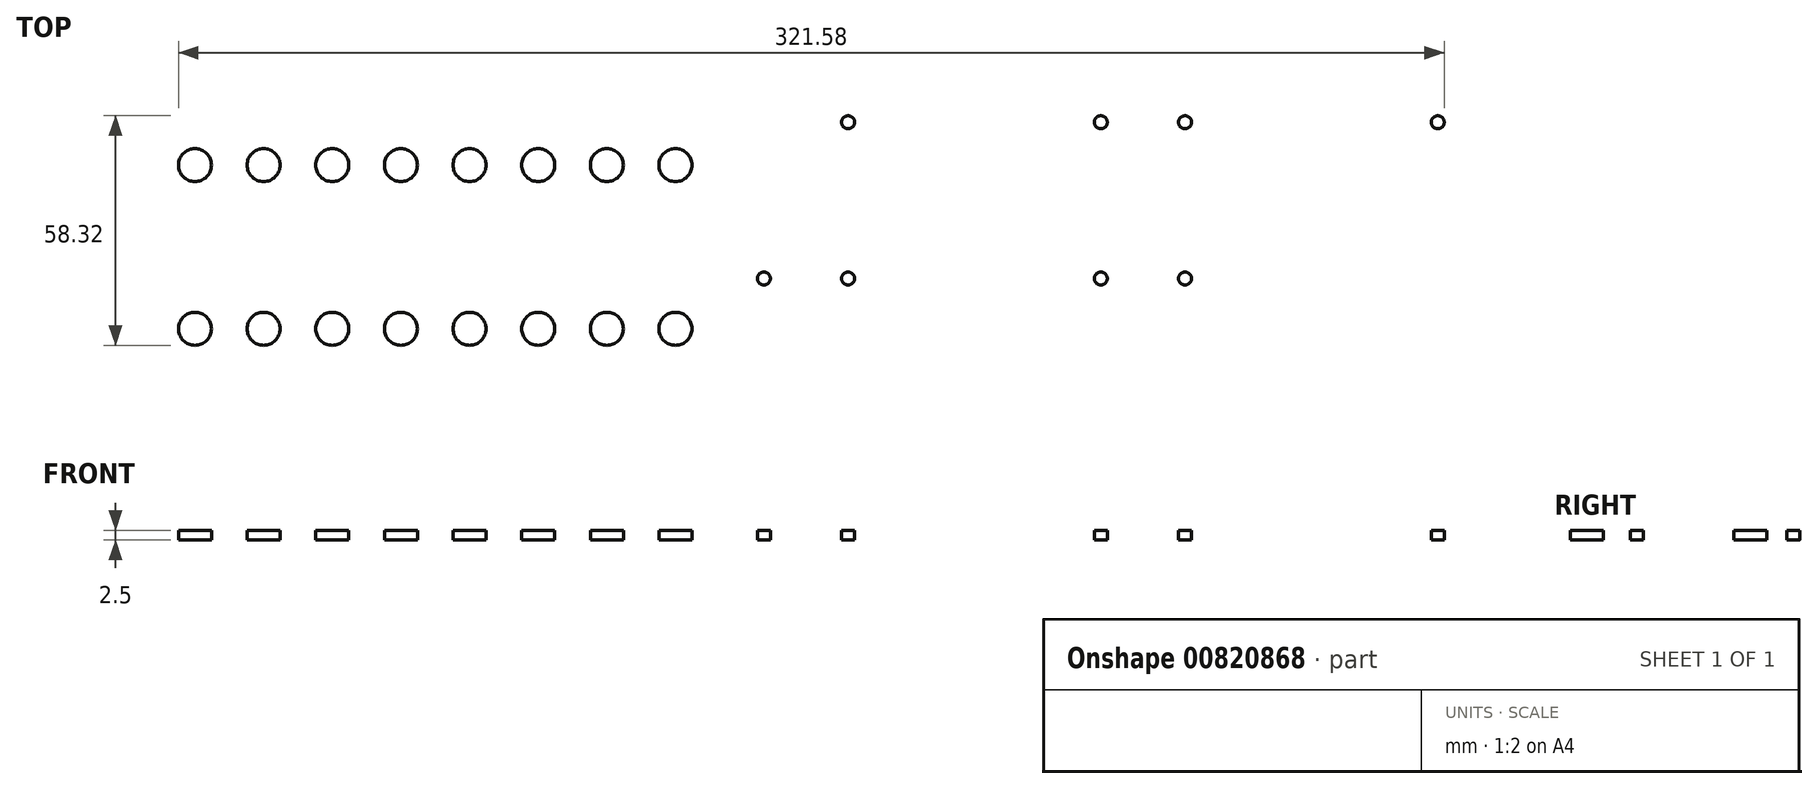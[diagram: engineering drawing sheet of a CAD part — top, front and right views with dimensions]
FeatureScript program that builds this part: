
annotation { "Feature Type Name" : "Feature", "Feature Type Description" : "" }
export const myFeature = defineFeature(function(context is Context, id is Id, definition is map)
    precondition{}
    {
        {
            var Q0;
            Q0=qCreatedBy(makeId("Top.planeOp"),FACE);
            var sketch = newSketch(context, id + "F0", { "sketchPlane" : qUnion([Q0])});
            skLineSegment(sketch, "E0.bottom", {"start": v(-66.95, 52.35) * mm, "end": v(415.65, 52.35) * mm});
            skLineSegment(sketch, "E0.top", {"start": v(-66.95, -36.55) * mm, "end": v(415.65, -36.55) * mm});
            skLineSegment(sketch, "E0.left", {"start": v(-66.95, 52.35) * mm, "end": v(-66.95, -36.55) * mm});
            skLineSegment(sketch, "E0.right", {"start": v(415.65, 52.35) * mm, "end": v(415.65, -36.55) * mm});
            skSolve(sketch);
        }
        {
            var Q0;
            Q0=makeQuery(id+"F0.imprint","IMPRINT",FACE,{"disambiguationData":[TD([[makeQuery(id+"F0.imprint","IMPRINT",EDGE,{"derivedFrom":sQuery(id+"F0.wireOp",EDGE,"E0.bottom")}),-1.0]])]});
            extrude(context, id + "F1", {"entities" : qUnion([Q0]), "depth" : 3 * mm, "offsetDistance" : 25 * mm});
        }
        {
            var Q0;
            Q0=makeQuery(id+"F1.opExtrude","CAP_FACE",FACE,{"disambiguationData":[OSD([sQuery(id+"F0.wireOp",EDGE,"E0.bottom"),sQuery(id+"F0.wireOp",EDGE,"E0.top"),sQuery(id+"F0.wireOp",EDGE,"E0.left"),sQuery(id+"F0.wireOp",EDGE,"E0.right")])],"isStart":false});
            var sketch = newSketch(context, id + "F2", { "sketchPlane" : qUnion([Q0])});
            skLineSegment(sketch, "E1.MirrorCS", {"start": v(-59.01, -1.97) * mm, "end": v(-61.51, -1.97) * mm});
            skLineSegment(sketch, "E2.MirrorCS", {"start": v(-59.01, -17.85) * mm, "end": v(-61.51, -17.85) * mm});
            skLineSegment(sketch, "E3.MirrorCS", {"start": v(-59.01, -17.85) * mm, "end": v(-56.51, -17.85) * mm});
            skLineSegment(sketch, "E4.MirrorCS", {"start": v(-59.01, -10.85) * mm, "end": v(-56.51, -10.85) * mm});
            skLineSegment(sketch, "E5.MirrorCS", {"start": v(-59.01, -10.85) * mm, "end": v(-61.51, -10.85) * mm});
            skLineSegment(sketch, "E6.MirrorCS", {"start": v(-59.01, -1.97) * mm, "end": v(-56.51, -1.97) * mm});
            skLineSegment(sketch, "E7.MirrorCS", {"start": v(-59.01, 5.03) * mm, "end": v(-61.51, 5.03) * mm});
            skLineSegment(sketch, "E8.MirrorCS", {"start": v(-59.01, 5.03) * mm, "end": v(-56.51, 5.03) * mm});
            skArc(sketch, "E9.MirrorCS", {"start": v(-61.51, -17.85) * mm, "mid": v(-64.01, -14.35) * mm, "end": v(-61.51, -10.85) * mm});
            skLineSegment(sketch, "E10.MirrorCS", {"start": v(-59.01, 49.5) * mm, "end": v(-61.51, 49.5) * mm});
            skArc(sketch, "E11.MirrorCS", {"start": v(-61.51, 33.62) * mm, "mid": v(-64.01, 30.12) * mm, "end": v(-61.51, 26.62) * mm});
            skPoint(sketch, "E12.MirrorP", {"position": v(-59.01, 1.55) * mm});
            skLineSegment(sketch, "E13.MirrorCS", {"start": v(-59.01, 17.75) * mm, "end": v(-56.51, 17.75) * mm});
            skLineSegment(sketch, "E14.MirrorCS", {"start": v(-59.01, 10.75) * mm, "end": v(-61.51, 10.75) * mm});
            skLineSegment(sketch, "E15.MirrorCS", {"start": v(-59.01, 17.75) * mm, "end": v(-61.51, 17.75) * mm});
            skPoint(sketch, "E16.MirrorP", {"position": v(-59.01, -14.33) * mm});
            skLineSegment(sketch, "E17.MirrorCS", {"start": v(-59.01, 49.5) * mm, "end": v(-56.51, 49.5) * mm});
            skLineSegment(sketch, "E18.MirrorCS", {"start": v(-59.01, 10.75) * mm, "end": v(-56.51, 10.75) * mm});
            skLineSegment(sketch, "E19.MirrorCS", {"start": v(-59.01, -26.72) * mm, "end": v(-56.51, -26.72) * mm});
            skLineSegment(sketch, "E20.MirrorCS", {"start": v(-59.01, 33.62) * mm, "end": v(-61.51, 33.62) * mm});
            skLineSegment(sketch, "E21.MirrorCS", {"start": v(-59.01, 26.62) * mm, "end": v(-56.51, 26.62) * mm});
            skPoint(sketch, "E22.MirrorP", {"position": v(-59.01, 1.53) * mm});
            skLineSegment(sketch, "E23.MirrorCS", {"start": v(-59.01, 33.62) * mm, "end": v(-56.51, 33.62) * mm});
            skLineSegment(sketch, "E24.MirrorCS", {"start": v(-59.01, -26.72) * mm, "end": v(-61.51, -26.72) * mm});
            skLineSegment(sketch, "E25.MirrorCS", {"start": v(-59.01, 26.62) * mm, "end": v(-61.51, 26.62) * mm});
            skArc(sketch, "E26.MirrorCS", {"start": v(-56.51, -10.85) * mm, "mid": v(-54.01, -14.35) * mm, "end": v(-56.51, -17.85) * mm});
            skPoint(sketch, "E27.MirrorP", {"position": v(-59.01, 30.12) * mm});
            skArc(sketch, "E28.MirrorCS", {"start": v(-56.51, -1.97) * mm, "mid": v(-54.01, 1.53) * mm, "end": v(-56.51, 5.03) * mm});
            skPoint(sketch, "E29.MirrorP", {"position": v(-59.01, -30.22) * mm});
            skArc(sketch, "E30.MirrorCS", {"start": v(-56.51, 26.62) * mm, "mid": v(-54.01, 30.12) * mm, "end": v(-56.51, 33.62) * mm});
            skLineSegment(sketch, "E31.MirrorCS", {"start": v(-59.01, -33.72) * mm, "end": v(-56.51, -33.72) * mm});
            skLineSegment(sketch, "E32.MirrorCS", {"start": v(-59.01, 42.5) * mm, "end": v(-61.51, 42.5) * mm});
            skLineSegment(sketch, "E33.MirrorCS", {"start": v(-59.01, 42.5) * mm, "end": v(-56.51, 42.5) * mm});
            skPoint(sketch, "E34.MirrorP", {"position": v(-59.01, -14.35) * mm});
            skLineSegment(sketch, "E35.MirrorCS", {"start": v(-59.01, -33.72) * mm, "end": v(-61.51, -33.72) * mm});
            skArc(sketch, "E36.MirrorCS", {"start": v(-61.51, 5.03) * mm, "mid": v(-64.01, 1.53) * mm, "end": v(-61.51, -1.97) * mm});
            skPoint(sketch, "E37.MirrorP", {"position": v(-59.01, 14.25) * mm});
            skPoint(sketch, "E38.MirrorP", {"position": v(1.07, 19.02) * mm});
            skCircle(sketch, "E39.MirrorC", {"center": v(170.96, 29.9) * mm, "radius": 1.65 * mm});
            skCircle(sketch, "E40.MirrorC", {"center": v(192.36, -9.8) * mm, "radius": 1.65 * mm});
            skCircle(sketch, "E41.MirrorC", {"center": v(256.56, -9.8) * mm, "radius": 1.65 * mm});
            skArc(sketch, "E42.MirrorCS", {"start": v(-56.51, 17.75) * mm, "mid": v(-54.01, 14.25) * mm, "end": v(-56.51, 10.75) * mm});
            skPoint(sketch, "E43.MirrorP", {"position": v(-16.37, 39.58) * mm});
            skCircle(sketch, "E44.MirrorC", {"center": v(170.96, -9.8) * mm, "radius": 1.65 * mm});
            skCircle(sketch, "E45.MirrorC", {"center": v(299.36, 29.9) * mm, "radius": 1.65 * mm});
            skCircle(sketch, "E46.MirrorC", {"center": v(149.56, -9.8) * mm, "radius": 1.65 * mm});
            skPoint(sketch, "E47.MirrorP", {"position": v(-16.37, 19.02) * mm});
            skPoint(sketch, "E48.MirrorP", {"position": v(1.07, -22.57) * mm});
            skPoint(sketch, "E49.MirrorP", {"position": v(1.07, 39.58) * mm});
            skCircle(sketch, "E50.MirrorC", {"center": v(128.16, -9.8) * mm, "radius": 1.65 * mm});
            skCircle(sketch, "E51.MirrorC", {"center": v(277.96, 29.9) * mm, "radius": 1.65 * mm});
            skCircle(sketch, "E52.MirrorC", {"center": v(192.36, 29.9) * mm, "radius": 1.65 * mm});
            skCircle(sketch, "E53.MirrorC", {"center": v(213.76, 29.9) * mm, "radius": 1.65 * mm});
            skPoint(sketch, "E54.MirrorP", {"position": v(-16.37, -2.01) * mm});
            skPoint(sketch, "E55.MirrorP", {"position": v(1.07, -2.01) * mm});
            skPoint(sketch, "E56.MirrorP", {"position": v(-59.01, 46) * mm});
            skCircle(sketch, "E57.MirrorC", {"center": v(213.76, -9.8) * mm, "radius": 1.65 * mm});
            skCircle(sketch, "E58.MirrorC", {"center": v(235.16, -9.8) * mm, "radius": 1.65 * mm});
            skCircle(sketch, "E59.MirrorC", {"center": v(235.16, 29.9) * mm, "radius": 1.65 * mm});
            skPoint(sketch, "E60.MirrorP", {"position": v(-59.01, -30.2) * mm});
            skPoint(sketch, "E61.MirrorP", {"position": v(-16.37, -22.57) * mm});
            skCircle(sketch, "E62.MirrorC", {"center": v(149.56, 29.9) * mm, "radius": 1.65 * mm});
            skCircle(sketch, "E63.MirrorC", {"center": v(256.56, 29.9) * mm, "radius": 1.65 * mm});
            skCircle(sketch, "E64.MirrorC", {"center": v(277.96, -9.8) * mm, "radius": 1.65 * mm});
            skCircle(sketch, "E65.MirrorC", {"center": v(35.95, 19.02) * mm, "radius": 4.2 * mm});
            skPoint(sketch, "E66.MirrorP", {"position": v(88.27, -22.57) * mm});
            skArc(sketch, "E67.MirrorCS", {"start": v(-56.51, -33.72) * mm, "mid": v(-54.01, -30.22) * mm, "end": v(-56.51, -26.72) * mm});
            skCircle(sketch, "E68.MirrorC", {"center": v(53.39, 39.58) * mm, "radius": 4.2 * mm});
            skPoint(sketch, "E69.MirrorP", {"position": v(105.7, 19.02) * mm});
            skPoint(sketch, "E70.MirrorP", {"position": v(18.5, 39.58) * mm});
            skCircle(sketch, "E71.MirrorC", {"center": v(-16.37, -2.01) * mm, "radius": 4.2 * mm});
            skCircle(sketch, "E72.MirrorC", {"center": v(-16.37, 39.58) * mm, "radius": 4.2 * mm});
            skCircle(sketch, "E73.MirrorC", {"center": v(-16.37, -22.57) * mm, "radius": 4.2 * mm});
            skCircle(sketch, "E74.MirrorC", {"center": v(1.07, -22.57) * mm, "radius": 4.2 * mm});
            skPoint(sketch, "E75.MirrorP", {"position": v(105.7, -2.01) * mm});
            skCircle(sketch, "E76.MirrorC", {"center": v(88.27, 19.02) * mm, "radius": 4.2 * mm});
            skCircle(sketch, "E77.MirrorC", {"center": v(35.95, 39.58) * mm, "radius": 4.2 * mm});
            skPoint(sketch, "E78.MirrorP", {"position": v(70.83, -2.01) * mm});
            skPoint(sketch, "E79.MirrorP", {"position": v(18.5, -2.01) * mm});
            skCircle(sketch, "E80.MirrorC", {"center": v(1.07, 19.02) * mm, "radius": 4.2 * mm});
            skArc(sketch, "E81.MirrorCS", {"start": v(-56.51, 49.5) * mm, "mid": v(-54.01, 46) * mm, "end": v(-56.51, 42.5) * mm});
            skCircle(sketch, "E82.MirrorC", {"center": v(35.95, -22.57) * mm, "radius": 4.2 * mm});
            skCircle(sketch, "E83.MirrorC", {"center": v(70.83, 39.58) * mm, "radius": 4.2 * mm});
            skPoint(sketch, "E84.MirrorP", {"position": v(70.83, 19.02) * mm});
            skPoint(sketch, "E85.MirrorP", {"position": v(53.39, -22.57) * mm});
            skCircle(sketch, "E86.MirrorC", {"center": v(-16.37, 19.02) * mm, "radius": 4.2 * mm});
            skArc(sketch, "E87.MirrorCS", {"start": v(-61.51, 10.75) * mm, "mid": v(-64.01, 14.25) * mm, "end": v(-61.51, 17.75) * mm});
            skArc(sketch, "E88.MirrorCS", {"start": v(-61.51, 42.5) * mm, "mid": v(-64.01, 46) * mm, "end": v(-61.51, 49.5) * mm});
            skCircle(sketch, "E89.MirrorC", {"center": v(70.83, 19.02) * mm, "radius": 4.2 * mm});
            skCircle(sketch, "E90.MirrorC", {"center": v(105.7, 19.02) * mm, "radius": 4.2 * mm});
            skCircle(sketch, "E91.MirrorC", {"center": v(88.27, 39.58) * mm, "radius": 4.2 * mm});
            skCircle(sketch, "E92.MirrorC", {"center": v(105.7, -22.57) * mm, "radius": 4.2 * mm});
            skPoint(sketch, "E93.MirrorP", {"position": v(88.27, -2.01) * mm});
            skArc(sketch, "E94.MirrorCS", {"start": v(-61.51, -26.72) * mm, "mid": v(-64.01, -30.22) * mm, "end": v(-61.51, -33.72) * mm});
            skCircle(sketch, "E95.MirrorC", {"center": v(88.27, -22.57) * mm, "radius": 4.2 * mm});
            skCircle(sketch, "E96.MirrorC", {"center": v(53.39, -22.57) * mm, "radius": 4.2 * mm});
            skPoint(sketch, "E97.MirrorP", {"position": v(53.39, -2.01) * mm});
            skPoint(sketch, "E98.MirrorP", {"position": v(35.95, -2.01) * mm});
            skCircle(sketch, "E99.MirrorC", {"center": v(18.5, 19.02) * mm, "radius": 4.2 * mm});
            skPoint(sketch, "E100.MirrorP", {"position": v(18.5, -22.57) * mm});
            skCircle(sketch, "E101.MirrorC", {"center": v(70.83, -22.57) * mm, "radius": 4.2 * mm});
            skCircle(sketch, "E102.MirrorC", {"center": v(88.27, -2.01) * mm, "radius": 4.2 * mm});
            skCircle(sketch, "E103.MirrorC", {"center": v(105.7, -2.01) * mm, "radius": 4.2 * mm});
            skPoint(sketch, "E104.MirrorP", {"position": v(53.39, 19.02) * mm});
            skCircle(sketch, "E105.MirrorC", {"center": v(1.07, 39.58) * mm, "radius": 4.2 * mm});
            skCircle(sketch, "E106.MirrorC", {"center": v(53.39, -2.01) * mm, "radius": 4.2 * mm});
            skCircle(sketch, "E107.MirrorC", {"center": v(70.83, -2.01) * mm, "radius": 4.2 * mm});
            skCircle(sketch, "E108.MirrorC", {"center": v(18.5, 39.58) * mm, "radius": 4.2 * mm});
            skCircle(sketch, "E109.MirrorC", {"center": v(105.7, 39.58) * mm, "radius": 4.2 * mm});
            skCircle(sketch, "E110.MirrorC", {"center": v(35.95, -2.01) * mm, "radius": 4.2 * mm});
            skCircle(sketch, "E111.MirrorC", {"center": v(18.5, -2.01) * mm, "radius": 4.2 * mm});
            skCircle(sketch, "E112.MirrorC", {"center": v(1.07, -2.01) * mm, "radius": 4.2 * mm});
            skCircle(sketch, "E113.MirrorC", {"center": v(18.5, -22.57) * mm, "radius": 4.2 * mm});
            skCircle(sketch, "E114.MirrorC", {"center": v(53.39, 19.02) * mm, "radius": 4.2 * mm});
            skLineSegment(sketch, "E115.MirrorCS", {"start": v(407.71, 5.03) * mm, "end": v(405.21, 5.03) * mm});
            skLineSegment(sketch, "E116.MirrorCS", {"start": v(407.71, 5.03) * mm, "end": v(410.21, 5.03) * mm});
            skLineSegment(sketch, "E117.MirrorCS", {"start": v(407.71, -10.85) * mm, "end": v(405.21, -10.85) * mm});
            skLineSegment(sketch, "E118.MirrorCS", {"start": v(407.71, -10.85) * mm, "end": v(410.21, -10.85) * mm});
            skLineSegment(sketch, "E119.MirrorCS", {"start": v(407.71, -1.97) * mm, "end": v(410.21, -1.97) * mm});
            skLineSegment(sketch, "E120.MirrorCS", {"start": v(407.71, -17.85) * mm, "end": v(410.21, -17.85) * mm});
            skLineSegment(sketch, "E121.MirrorCS", {"start": v(407.71, -1.97) * mm, "end": v(405.21, -1.97) * mm});
            skLineSegment(sketch, "E122.MirrorCS", {"start": v(407.71, -17.85) * mm, "end": v(405.21, -17.85) * mm});
            skPoint(sketch, "E123.MirrorP", {"position": v(407.71, 1.55) * mm});
            skArc(sketch, "E124.MirrorCS", {"start": v(410.21, -17.85) * mm, "mid": v(412.71, -14.35) * mm, "end": v(410.21, -10.85) * mm});
            skLineSegment(sketch, "E125.MirrorCS", {"start": v(407.71, -26.72) * mm, "end": v(405.21, -26.72) * mm});
            skLineSegment(sketch, "E126.MirrorCS", {"start": v(407.71, -33.72) * mm, "end": v(410.21, -33.72) * mm});
            skPoint(sketch, "E127.MirrorP", {"position": v(407.71, -14.33) * mm});
            skArc(sketch, "E128.MirrorCS", {"start": v(410.21, 33.62) * mm, "mid": v(412.71, 30.12) * mm, "end": v(410.21, 26.62) * mm});
            skLineSegment(sketch, "E129.MirrorCS", {"start": v(407.71, -33.72) * mm, "end": v(405.21, -33.72) * mm});
            skLineSegment(sketch, "E130.MirrorCS", {"start": v(407.71, -26.72) * mm, "end": v(410.21, -26.72) * mm});
            skLineSegment(sketch, "E131.MirrorCS", {"start": v(407.71, 42.5) * mm, "end": v(410.21, 42.5) * mm});
            skLineSegment(sketch, "E132.MirrorCS", {"start": v(407.71, 42.5) * mm, "end": v(405.21, 42.5) * mm});
            skLineSegment(sketch, "E133.MirrorCS", {"start": v(407.71, 10.75) * mm, "end": v(405.21, 10.75) * mm});
            skPoint(sketch, "E134.MirrorP", {"position": v(407.71, -14.35) * mm});
            skLineSegment(sketch, "E135.MirrorCS", {"start": v(407.71, 49.5) * mm, "end": v(405.21, 49.5) * mm});
            skPoint(sketch, "E136.MirrorP", {"position": v(407.71, -30.2) * mm});
            skLineSegment(sketch, "E137.MirrorCS", {"start": v(407.71, 33.62) * mm, "end": v(410.21, 33.62) * mm});
            skLineSegment(sketch, "E138.MirrorCS", {"start": v(407.71, 10.75) * mm, "end": v(410.21, 10.75) * mm});
            skLineSegment(sketch, "E139.MirrorCS", {"start": v(407.71, 17.75) * mm, "end": v(410.21, 17.75) * mm});
            skLineSegment(sketch, "E140.MirrorCS", {"start": v(407.71, 17.75) * mm, "end": v(405.21, 17.75) * mm});
            skLineSegment(sketch, "E141.MirrorCS", {"start": v(407.71, 33.62) * mm, "end": v(405.21, 33.62) * mm});
            skLineSegment(sketch, "E142.MirrorCS", {"start": v(407.71, 26.62) * mm, "end": v(405.21, 26.62) * mm});
            skLineSegment(sketch, "E143.MirrorCS", {"start": v(407.71, 49.5) * mm, "end": v(410.21, 49.5) * mm});
            skLineSegment(sketch, "E144.MirrorCS", {"start": v(407.71, 26.62) * mm, "end": v(410.21, 26.62) * mm});
            skPoint(sketch, "E145.MirrorP", {"position": v(407.71, 1.53) * mm});
            skArc(sketch, "E146.MirrorCS", {"start": v(405.21, -33.72) * mm, "mid": v(402.71, -30.22) * mm, "end": v(405.21, -26.72) * mm});
            skPoint(sketch, "E147.MirrorP", {"position": v(407.71, 46) * mm});
            skPoint(sketch, "E148.MirrorP", {"position": v(407.71, 14.25) * mm});
            skArc(sketch, "E149.MirrorCS", {"start": v(410.21, 10.75) * mm, "mid": v(412.71, 14.25) * mm, "end": v(410.21, 17.75) * mm});
            skPoint(sketch, "E150.MirrorP", {"position": v(407.71, 30.12) * mm});
            skArc(sketch, "E151.MirrorCS", {"start": v(405.21, -1.97) * mm, "mid": v(402.71, 1.53) * mm, "end": v(405.21, 5.03) * mm});
            skArc(sketch, "E152.MirrorCS", {"start": v(405.21, -10.85) * mm, "mid": v(402.71, -14.35) * mm, "end": v(405.21, -17.85) * mm});
            skArc(sketch, "E153.MirrorCS", {"start": v(405.21, 49.5) * mm, "mid": v(402.71, 46) * mm, "end": v(405.21, 42.5) * mm});
            skArc(sketch, "E154.MirrorCS", {"start": v(410.21, -26.72) * mm, "mid": v(412.71, -30.22) * mm, "end": v(410.21, -33.72) * mm});
            skArc(sketch, "E155.MirrorCS", {"start": v(405.21, 26.62) * mm, "mid": v(402.71, 30.12) * mm, "end": v(405.21, 33.62) * mm});
            skArc(sketch, "E156.MirrorCS", {"start": v(410.21, 42.5) * mm, "mid": v(412.71, 46) * mm, "end": v(410.21, 49.5) * mm});
            skArc(sketch, "E157.MirrorCS", {"start": v(405.21, 17.75) * mm, "mid": v(402.71, 14.25) * mm, "end": v(405.21, 10.75) * mm});
            skArc(sketch, "E158.MirrorCS", {"start": v(410.21, 5.03) * mm, "mid": v(412.71, 1.53) * mm, "end": v(410.21, -1.97) * mm});
            skPoint(sketch, "E159.MirrorP", {"position": v(407.71, -30.22) * mm});
            skSolve(sketch);
        }
        {
            var Q0;
            Q0=makeQuery(id+"F2.imprint","IMPRINT",FACE,{"disambiguationData":[TD([[makeQuery(id+"F2.imprint","IMPRINT",EDGE,{"derivedFrom":sQuery(id+"F2.wireOp",EDGE,"E19.MirrorCS")}),-1.0]])]});
            var Q1;
            Q1=makeQuery(id+"F2.imprint","IMPRINT",FACE,{"disambiguationData":[TD([[makeQuery(id+"F2.imprint","IMPRINT",EDGE,{"derivedFrom":sQuery(id+"F2.wireOp",EDGE,"E10.MirrorCS")}),1.0]])]});
            var Q2;
            Q2=makeQuery(id+"F2.imprint","IMPRINT",FACE,{"disambiguationData":[TD([[makeQuery(id+"F2.imprint","IMPRINT",EDGE,{"derivedFrom":sQuery(id+"F2.wireOp",EDGE,"E13.MirrorCS")}),-1.0]])]});
            var Q3;
            Q3=makeQuery(id+"F2.imprint","IMPRINT",FACE,{"disambiguationData":[TD([[makeQuery(id+"F2.imprint","IMPRINT",EDGE,{"derivedFrom":sQuery(id+"F2.wireOp",EDGE,"E2.MirrorCS")}),-1.0]])]});
            var Q4;
            Q4=makeQuery(id+"F2.imprint","IMPRINT",FACE,{"disambiguationData":[TD([[makeQuery(id+"F2.imprint","IMPRINT",EDGE,{"derivedFrom":sQuery(id+"F2.wireOp",EDGE,"E1.MirrorCS")}),-1.0]])]});
            var Q5;
            Q5=makeQuery(id+"F2.imprint","IMPRINT",FACE,{"disambiguationData":[TD([[makeQuery(id+"F2.imprint","IMPRINT",EDGE,{"derivedFrom":sQuery(id+"F2.wireOp",EDGE,"E20.MirrorCS")}),1.0]])]});
            var Q6;
            Q6=makeQuery(id+"F2.imprint","IMPRINT",FACE,{"disambiguationData":[TD([[makeQuery(id+"F2.imprint","IMPRINT",EDGE,{"derivedFrom":sQuery(id+"F2.wireOp",EDGE,"E83.MirrorC")}),1.0]])]});
            var Q7;
            Q7=makeQuery(id+"F2.imprint","IMPRINT",FACE,{"disambiguationData":[TD([[makeQuery(id+"F2.imprint","IMPRINT",EDGE,{"derivedFrom":sQuery(id+"F2.wireOp",EDGE,"E80.MirrorC")}),-1.0]])]});
            var Q8;
            Q8=makeQuery(id+"F2.imprint","IMPRINT",FACE,{"disambiguationData":[TD([[makeQuery(id+"F2.imprint","IMPRINT",EDGE,{"derivedFrom":sQuery(id+"F2.wireOp",EDGE,"E101.MirrorC")}),-1.0]])]});
            var Q9;
            Q9=makeQuery(id+"F2.imprint","IMPRINT",FACE,{"disambiguationData":[TD([[makeQuery(id+"F2.imprint","IMPRINT",EDGE,{"derivedFrom":sQuery(id+"F2.wireOp",EDGE,"E74.MirrorC")}),-1.0]])]});
            var Q10;
            Q10=makeQuery(id+"F2.imprint","IMPRINT",FACE,{"disambiguationData":[TD([[makeQuery(id+"F2.imprint","IMPRINT",EDGE,{"derivedFrom":sQuery(id+"F2.wireOp",EDGE,"E105.MirrorC")}),1.0]])]});
            var Q11;
            Q11=makeQuery(id+"F2.imprint","IMPRINT",FACE,{"disambiguationData":[TD([[makeQuery(id+"F2.imprint","IMPRINT",EDGE,{"derivedFrom":sQuery(id+"F2.wireOp",EDGE,"E107.MirrorC")}),1.0]])]});
            var Q12;
            Q12=makeQuery(id+"F2.imprint","IMPRINT",FACE,{"disambiguationData":[TD([[makeQuery(id+"F2.imprint","IMPRINT",EDGE,{"derivedFrom":sQuery(id+"F2.wireOp",EDGE,"E95.MirrorC")}),-1.0]])]});
            var Q13;
            Q13=makeQuery(id+"F2.imprint","IMPRINT",FACE,{"disambiguationData":[TD([[makeQuery(id+"F2.imprint","IMPRINT",EDGE,{"derivedFrom":sQuery(id+"F2.wireOp",EDGE,"E65.MirrorC")}),-1.0]])]});
            var Q14;
            Q14=makeQuery(id+"F2.imprint","IMPRINT",FACE,{"disambiguationData":[TD([[makeQuery(id+"F2.imprint","IMPRINT",EDGE,{"derivedFrom":sQuery(id+"F2.wireOp",EDGE,"E76.MirrorC")}),-1.0]])]});
            var Q15;
            Q15=makeQuery(id+"F2.imprint","IMPRINT",FACE,{"disambiguationData":[TD([[makeQuery(id+"F2.imprint","IMPRINT",EDGE,{"derivedFrom":sQuery(id+"F2.wireOp",EDGE,"E99.MirrorC")}),-1.0]])]});
            var Q16;
            Q16=makeQuery(id+"F2.imprint","IMPRINT",FACE,{"disambiguationData":[TD([[makeQuery(id+"F2.imprint","IMPRINT",EDGE,{"derivedFrom":sQuery(id+"F2.wireOp",EDGE,"E114.MirrorC")}),-1.0]])]});
            var Q17;
            Q17=makeQuery(id+"F2.imprint","IMPRINT",FACE,{"disambiguationData":[TD([[makeQuery(id+"F2.imprint","IMPRINT",EDGE,{"derivedFrom":sQuery(id+"F2.wireOp",EDGE,"E92.MirrorC")}),-1.0]])]});
            var Q18;
            Q18=makeQuery(id+"F2.imprint","IMPRINT",FACE,{"disambiguationData":[TD([[makeQuery(id+"F2.imprint","IMPRINT",EDGE,{"derivedFrom":sQuery(id+"F2.wireOp",EDGE,"E68.MirrorC")}),1.0]])]});
            var Q19;
            Q19=makeQuery(id+"F2.imprint","IMPRINT",FACE,{"disambiguationData":[TD([[makeQuery(id+"F2.imprint","IMPRINT",EDGE,{"derivedFrom":sQuery(id+"F2.wireOp",EDGE,"E72.MirrorC")}),1.0]])]});
            var Q20;
            Q20=makeQuery(id+"F2.imprint","IMPRINT",FACE,{"disambiguationData":[TD([[makeQuery(id+"F2.imprint","IMPRINT",EDGE,{"derivedFrom":sQuery(id+"F2.wireOp",EDGE,"E91.MirrorC")}),1.0]])]});
            var Q21;
            Q21=makeQuery(id+"F2.imprint","IMPRINT",FACE,{"disambiguationData":[TD([[makeQuery(id+"F2.imprint","IMPRINT",EDGE,{"derivedFrom":sQuery(id+"F2.wireOp",EDGE,"E113.MirrorC")}),-1.0]])]});
            var Q22;
            Q22=makeQuery(id+"F2.imprint","IMPRINT",FACE,{"disambiguationData":[TD([[makeQuery(id+"F2.imprint","IMPRINT",EDGE,{"derivedFrom":sQuery(id+"F2.wireOp",EDGE,"E106.MirrorC")}),1.0]])]});
            var Q23;
            Q23=makeQuery(id+"F2.imprint","IMPRINT",FACE,{"disambiguationData":[TD([[makeQuery(id+"F2.imprint","IMPRINT",EDGE,{"derivedFrom":sQuery(id+"F2.wireOp",EDGE,"E73.MirrorC")}),-1.0]])]});
            var Q24;
            Q24=makeQuery(id+"F2.imprint","IMPRINT",FACE,{"disambiguationData":[TD([[makeQuery(id+"F2.imprint","IMPRINT",EDGE,{"derivedFrom":sQuery(id+"F2.wireOp",EDGE,"E102.MirrorC")}),1.0]])]});
            var Q25;
            Q25=makeQuery(id+"F2.imprint","IMPRINT",FACE,{"disambiguationData":[TD([[makeQuery(id+"F2.imprint","IMPRINT",EDGE,{"derivedFrom":sQuery(id+"F2.wireOp",EDGE,"E96.MirrorC")}),-1.0]])]});
            var Q26;
            Q26=makeQuery(id+"F2.imprint","IMPRINT",FACE,{"disambiguationData":[TD([[makeQuery(id+"F2.imprint","IMPRINT",EDGE,{"derivedFrom":sQuery(id+"F2.wireOp",EDGE,"E77.MirrorC")}),1.0]])]});
            var Q27;
            Q27=makeQuery(id+"F2.imprint","IMPRINT",FACE,{"disambiguationData":[TD([[makeQuery(id+"F2.imprint","IMPRINT",EDGE,{"derivedFrom":sQuery(id+"F2.wireOp",EDGE,"E110.MirrorC")}),1.0]])]});
            var Q28;
            Q28=makeQuery(id+"F2.imprint","IMPRINT",FACE,{"disambiguationData":[TD([[makeQuery(id+"F2.imprint","IMPRINT",EDGE,{"derivedFrom":sQuery(id+"F2.wireOp",EDGE,"E109.MirrorC")}),1.0]])]});
            var Q29;
            Q29=makeQuery(id+"F2.imprint","IMPRINT",FACE,{"disambiguationData":[TD([[makeQuery(id+"F2.imprint","IMPRINT",EDGE,{"derivedFrom":sQuery(id+"F2.wireOp",EDGE,"E86.MirrorC")}),-1.0]])]});
            var Q30;
            Q30=makeQuery(id+"F2.imprint","IMPRINT",FACE,{"disambiguationData":[TD([[makeQuery(id+"F2.imprint","IMPRINT",EDGE,{"derivedFrom":sQuery(id+"F2.wireOp",EDGE,"E89.MirrorC")}),-1.0]])]});
            var Q31;
            Q31=makeQuery(id+"F2.imprint","IMPRINT",FACE,{"disambiguationData":[TD([[makeQuery(id+"F2.imprint","IMPRINT",EDGE,{"derivedFrom":sQuery(id+"F2.wireOp",EDGE,"E111.MirrorC")}),1.0]])]});
            var Q32;
            Q32=makeQuery(id+"F2.imprint","IMPRINT",FACE,{"disambiguationData":[TD([[makeQuery(id+"F2.imprint","IMPRINT",EDGE,{"derivedFrom":sQuery(id+"F2.wireOp",EDGE,"E90.MirrorC")}),-1.0]])]});
            var Q33;
            Q33=makeQuery(id+"F2.imprint","IMPRINT",FACE,{"disambiguationData":[TD([[makeQuery(id+"F2.imprint","IMPRINT",EDGE,{"derivedFrom":sQuery(id+"F2.wireOp",EDGE,"E108.MirrorC")}),1.0]])]});
            var Q34;
            Q34=makeQuery(id+"F2.imprint","IMPRINT",FACE,{"disambiguationData":[TD([[makeQuery(id+"F2.imprint","IMPRINT",EDGE,{"derivedFrom":sQuery(id+"F2.wireOp",EDGE,"E82.MirrorC")}),-1.0]])]});
            var Q35;
            Q35=makeQuery(id+"F2.imprint","IMPRINT",FACE,{"disambiguationData":[TD([[makeQuery(id+"F2.imprint","IMPRINT",EDGE,{"derivedFrom":sQuery(id+"F2.wireOp",EDGE,"E46.MirrorC")}),-1.0]])]});
            var Q36;
            Q36=makeQuery(id+"F2.imprint","IMPRINT",FACE,{"disambiguationData":[TD([[makeQuery(id+"F2.imprint","IMPRINT",EDGE,{"derivedFrom":sQuery(id+"F2.wireOp",EDGE,"E40.MirrorC")}),1.0]])]});
            var Q37;
            Q37=makeQuery(id+"F2.imprint","IMPRINT",FACE,{"disambiguationData":[TD([[makeQuery(id+"F2.imprint","IMPRINT",EDGE,{"derivedFrom":sQuery(id+"F2.wireOp",EDGE,"E45.MirrorC")}),-1.0]])]});
            var Q38;
            Q38=makeQuery(id+"F2.imprint","IMPRINT",FACE,{"disambiguationData":[TD([[makeQuery(id+"F2.imprint","IMPRINT",EDGE,{"derivedFrom":sQuery(id+"F2.wireOp",EDGE,"E50.MirrorC")}),-1.0]])]});
            var Q39;
            Q39=makeQuery(id+"F2.imprint","IMPRINT",FACE,{"disambiguationData":[TD([[makeQuery(id+"F2.imprint","IMPRINT",EDGE,{"derivedFrom":sQuery(id+"F2.wireOp",EDGE,"E58.MirrorC")}),-1.0]])]});
            var Q40;
            Q40=makeQuery(id+"F2.imprint","IMPRINT",FACE,{"disambiguationData":[TD([[makeQuery(id+"F2.imprint","IMPRINT",EDGE,{"derivedFrom":sQuery(id+"F2.wireOp",EDGE,"E63.MirrorC")}),1.0]])]});
            var Q41;
            Q41=makeQuery(id+"F2.imprint","IMPRINT",FACE,{"disambiguationData":[TD([[makeQuery(id+"F2.imprint","IMPRINT",EDGE,{"derivedFrom":sQuery(id+"F2.wireOp",EDGE,"E51.MirrorC")}),1.0]])]});
            var Q42;
            Q42=makeQuery(id+"F2.imprint","IMPRINT",FACE,{"disambiguationData":[TD([[makeQuery(id+"F2.imprint","IMPRINT",EDGE,{"derivedFrom":sQuery(id+"F2.wireOp",EDGE,"E53.MirrorC")}),-1.0]])]});
            var Q43;
            Q43=makeQuery(id+"F2.imprint","IMPRINT",FACE,{"disambiguationData":[TD([[makeQuery(id+"F2.imprint","IMPRINT",EDGE,{"derivedFrom":sQuery(id+"F2.wireOp",EDGE,"E103.MirrorC")}),1.0]])]});
            var Q44;
            Q44=makeQuery(id+"F2.imprint","IMPRINT",FACE,{"disambiguationData":[TD([[makeQuery(id+"F2.imprint","IMPRINT",EDGE,{"derivedFrom":sQuery(id+"F2.wireOp",EDGE,"E62.MirrorC")}),-1.0]])]});
            var Q45;
            Q45=makeQuery(id+"F2.imprint","IMPRINT",FACE,{"disambiguationData":[TD([[makeQuery(id+"F2.imprint","IMPRINT",EDGE,{"derivedFrom":sQuery(id+"F2.wireOp",EDGE,"E64.MirrorC")}),1.0]])]});
            var Q46;
            Q46=makeQuery(id+"F2.imprint","IMPRINT",FACE,{"disambiguationData":[TD([[makeQuery(id+"F2.imprint","IMPRINT",EDGE,{"derivedFrom":sQuery(id+"F2.wireOp",EDGE,"E112.MirrorC")}),1.0]])]});
            var Q47;
            Q47=makeQuery(id+"F2.imprint","IMPRINT",FACE,{"disambiguationData":[TD([[makeQuery(id+"F2.imprint","IMPRINT",EDGE,{"derivedFrom":sQuery(id+"F2.wireOp",EDGE,"E39.MirrorC")}),1.0]])]});
            var Q48;
            Q48=makeQuery(id+"F2.imprint","IMPRINT",FACE,{"disambiguationData":[TD([[makeQuery(id+"F2.imprint","IMPRINT",EDGE,{"derivedFrom":sQuery(id+"F2.wireOp",EDGE,"E57.MirrorC")}),-1.0]])]});
            var Q49;
            Q49=makeQuery(id+"F2.imprint","IMPRINT",FACE,{"disambiguationData":[TD([[makeQuery(id+"F2.imprint","IMPRINT",EDGE,{"derivedFrom":sQuery(id+"F2.wireOp",EDGE,"E41.MirrorC")}),1.0]])]});
            var Q50;
            Q50=makeQuery(id+"F2.imprint","IMPRINT",FACE,{"disambiguationData":[TD([[makeQuery(id+"F2.imprint","IMPRINT",EDGE,{"derivedFrom":sQuery(id+"F2.wireOp",EDGE,"E52.MirrorC")}),1.0]])]});
            var Q51;
            Q51=makeQuery(id+"F2.imprint","IMPRINT",FACE,{"disambiguationData":[TD([[makeQuery(id+"F2.imprint","IMPRINT",EDGE,{"derivedFrom":sQuery(id+"F2.wireOp",EDGE,"E44.MirrorC")}),1.0]])]});
            var Q52;
            Q52=makeQuery(id+"F2.imprint","IMPRINT",FACE,{"disambiguationData":[TD([[makeQuery(id+"F2.imprint","IMPRINT",EDGE,{"derivedFrom":sQuery(id+"F2.wireOp",EDGE,"E59.MirrorC")}),-1.0]])]});
            var Q53;
            Q53=makeQuery(id+"F2.imprint","IMPRINT",FACE,{"disambiguationData":[TD([[makeQuery(id+"F2.imprint","IMPRINT",EDGE,{"derivedFrom":sQuery(id+"F2.wireOp",EDGE,"E71.MirrorC")}),1.0]])]});
            var Q54;
            Q54=makeQuery(id+"F2.imprint","IMPRINT",FACE,{"disambiguationData":[TD([[makeQuery(id+"F2.imprint","IMPRINT",EDGE,{"derivedFrom":sQuery(id+"F2.wireOp",EDGE,"E137.MirrorCS")}),-1.0]])]});
            var Q55;
            Q55=makeQuery(id+"F2.imprint","IMPRINT",FACE,{"disambiguationData":[TD([[makeQuery(id+"F2.imprint","IMPRINT",EDGE,{"derivedFrom":sQuery(id+"F2.wireOp",EDGE,"E117.MirrorCS")}),1.0]])]});
            var Q56;
            Q56=makeQuery(id+"F2.imprint","IMPRINT",FACE,{"disambiguationData":[TD([[makeQuery(id+"F2.imprint","IMPRINT",EDGE,{"derivedFrom":sQuery(id+"F2.wireOp",EDGE,"E115.MirrorCS")}),1.0]])]});
            var Q57;
            Q57=makeQuery(id+"F2.imprint","IMPRINT",FACE,{"disambiguationData":[TD([[makeQuery(id+"F2.imprint","IMPRINT",EDGE,{"derivedFrom":sQuery(id+"F2.wireOp",EDGE,"E133.MirrorCS")}),-1.0]])]});
            var Q58;
            Q58=makeQuery(id+"F2.imprint","IMPRINT",FACE,{"disambiguationData":[TD([[makeQuery(id+"F2.imprint","IMPRINT",EDGE,{"derivedFrom":sQuery(id+"F2.wireOp",EDGE,"E125.MirrorCS")}),1.0]])]});
            var Q59;
            Q59=makeQuery(id+"F2.imprint","IMPRINT",FACE,{"disambiguationData":[TD([[makeQuery(id+"F2.imprint","IMPRINT",EDGE,{"derivedFrom":sQuery(id+"F2.wireOp",EDGE,"E131.MirrorCS")}),1.0]])]});
            extrude(context, id + "F3", {"entities" : qUnion([Q0, Q1, Q2, Q3, Q4, Q5, Q6, Q7, Q8, Q9, Q10, Q11, Q12, Q13, Q14, Q15, Q16, Q17, Q18, Q19, Q20, Q21, Q22, Q23, Q24, Q25, Q26, Q27, Q28, Q29, Q30, Q31, Q32, Q33, Q34, Q35, Q36, Q37, Q38, Q39, Q40, Q41, Q42, Q43, Q44, Q45, Q46, Q47, Q48, Q49, Q50, Q51, Q52, Q53, Q54, Q55, Q56, Q57, Q58, Q59]), "operationType" : NewBodyOperationType.REMOVE, "oppositeDirection" : true, "depth" : 3 * mm, "offsetDistance" : 25 * mm});
        }
        {
            var Q0;
            Q0 = qSketchRegion(id + "F2", true);
            extrude(context, id + "F4", {"entities" : qUnion([Q0]), "operationType" : NewBodyOperationType.REMOVE, "oppositeDirection" : true, "depth" : 0.5 * mm, "offsetDistance" : 25 * mm});
        }
    });
